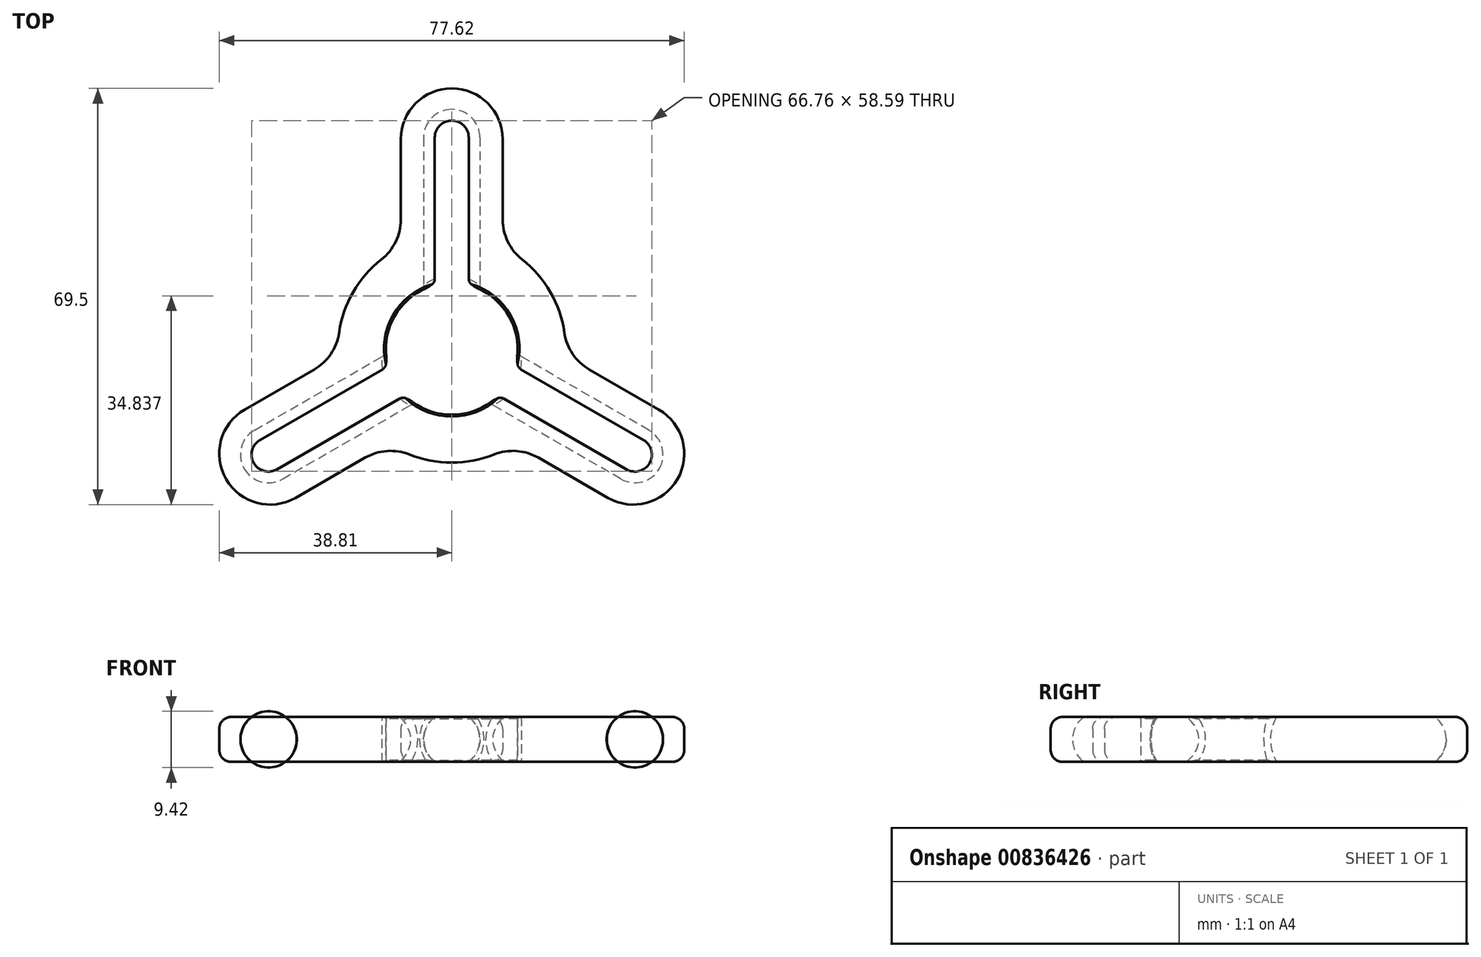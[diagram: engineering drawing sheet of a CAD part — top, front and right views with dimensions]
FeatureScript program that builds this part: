
annotation { "Feature Type Name" : "Feature", "Feature Type Description" : "" }
export const myFeature = defineFeature(function(context is Context, id is Id, definition is map)
    precondition{}
    {
        {
            var Q0;
            Q0=qCreatedBy(makeId("Top.planeOp"),FACE);
            var sketch = newSketch(context, id + "F0", { "sketchPlane" : qUnion([Q0])});
            skLineSegment(sketch, "E0", {"start": v(-9.53, 5.5) * mm, "end": v(0, 0) * mm, "construction": true});
            skLineSegment(sketch, "E1", {"start": v(0, 0) * mm, "end": v(9.53, 5.5) * mm, "construction": true});
            skArc(sketch, "E2", {"start": v(9.53, 5.5) * mm, "mid": v(0, 11) * mm, "end": v(-9.53, 5.5) * mm});
            skLineSegment(sketch, "E3", {"start": v(0, 0) * mm, "end": v(0, 11) * mm, "construction": true});
            skLineSegment(sketch, "E4", {"start": v(-9.53, 5.5) * mm, "end": v(-16.45, 9.5) * mm});
            skLineSegment(sketch, "E5", {"start": v(9.53, 5.5) * mm, "end": v(21.03, 12.14) * mm});
            skLineSegment(sketch, "E6", {"start": v(-8.5, 17) * mm, "end": v(-8.5, 35) * mm});
            skLineSegment(sketch, "E7", {"start": v(8.5, 35) * mm, "end": v(8.5, 17) * mm});
            skArc(sketch, "E8", {"start": v(-16.45, 9.5) * mm, "mid": v(-13.03, 13.83) * mm, "end": v(-8.5, 17) * mm});
            skArc(sketch, "E9", {"start": v(-8.5, 35) * mm, "mid": v(0, 43.5) * mm, "end": v(8.5, 35) * mm});
            skArc(sketch, "E10.trimOffspring", {"start": v(8.5, 17) * mm, "mid": v(13.03, 13.83) * mm, "end": v(16.45, 9.5) * mm});
            skSolve(sketch);
        }
        {
            var Q0;
            Q0=qSketchRegion(id+"F0",true);
            extrude(context, id + "F1", {"entities" : qUnion([Q0]), "depth" : 3.75 * mm, "offsetDistance" : 25 * mm, "hasSecondDirection" : true, "secondDirectionOppositeDirection" : true, "secondDirectionDepth" : 3.75 * mm});
        }
        {
            var Q0;
            Q0=qCreatedBy(makeId("Front.planeOp"),FACE);
            var sketch = newSketch(context, id + "F2", { "sketchPlane" : qUnion([Q0])});
            skCircle(sketch, "E11", {"center": v(0, 0) * mm, "radius": 4.7 * mm});
            skSolve(sketch);
        }
        {
            var Q0;
            Q0=qCreatedBy(makeId("Front.planeOp"),FACE);
            var sketch = newSketch(context, id + "F3", { "sketchPlane" : qUnion([Q0])});
            skLineSegment(sketch, "E12", {"start": v(0, 0) * mm, "end": v(0, 24.93) * mm});
            skSolve(sketch);
        }
        {
            var Q0;
            Q0=qSketchRegion(id+"F2",true);
            extrude(context, id + "F4", {"entities" : qUnion([Q0]), "oppositeDirection" : true, "depth" : 40 * mm, "offsetDistance" : 25 * mm});
        }
        {
            var Q0;
            Q0=makeQuery(id+"F4.opExtrude","CAP_EDGE",EDGE,{"disambiguationData":[OSD([sQuery(id+"F2.wireOp",EDGE,"E11")])],"isStart":false});
            fillet(context, id + "F5", {"entities" : qUnion([Q0]), "radius" : 4.7 * mm, "tangentPropagation" : true, "allowEdgeOverflow" : false});
        }
        {
            var Q0;
            Q0=makeQuery(id+"F1.opExtrude","SWEPT_EDGE",EDGE,{"disambiguationData":[OSD([sQuery(id+"F0.wireOp",EDGE,"E6"),sQuery(id+"F0.wireOp",EDGE,"E8")])]});
            var Q1;
            Q1=makeQuery(id+"F1.opExtrude","SWEPT_EDGE",EDGE,{"disambiguationData":[OSD([sQuery(id+"F0.wireOp",EDGE,"E7"),sQuery(id+"F0.wireOp",EDGE,"E10.trimOffspring")])]});
            fillet(context, id + "F6", {"entities" : qUnion([Q0, Q1]), "radius" : 8.5 * mm, "tangentPropagation" : true, "allowEdgeOverflow" : false});
        }
        {
            var Q0;
            Q0=makeQuery(id+"F4.opExtrude","SWEPT_BODY",BODY,{"disambiguationData":[OSD([sQuery(id+"F2.wireOp",EDGE,"E11")])]});
            var Q1;
            Q1=makeQuery(id+"F1.opExtrude","SWEPT_BODY",BODY,{"disambiguationData":[OSD([sQuery(id+"F0.wireOp",EDGE,"E2"),sQuery(id+"F0.wireOp",EDGE,"E4"),sQuery(id+"F0.wireOp",EDGE,"E5"),sQuery(id+"F0.wireOp",EDGE,"E6"),sQuery(id+"F0.wireOp",EDGE,"E7"),sQuery(id+"F0.wireOp",EDGE,"E8"),sQuery(id+"F0.wireOp",EDGE,"E9"),sQuery(id+"F0.wireOp",EDGE,"E10.trimOffspring")])]});
            booleanBodies(context, id + "F7", {"operationType" : BooleanOperationType.SUBTRACTION, "tools" : qUnion([Q0]), "targets" : qUnion([Q1])});
        }
        {
            var Q0;
            {var subQ0=sQuery(id+"F0.wireOp",EDGE,"E2");var subQ1=sQuery(id+"F0.wireOp",EDGE,"E4");Q0=makeQuery(id+"F7.opBoolean","SPLIT",EDGE,{"disambiguationData":[TD([makeQuery(id+"F1.opExtrude","SWEPT_FACE",FACE,{"disambiguationData":[OSD([subQ1])]})])],"derivedFrom":makeQuery(id+"F1.opExtrude","CAP_EDGE",EDGE,{"disambiguationData":[OSD([subQ0])],"isStart":false})});}
            var Q1;
            {var subQ0=sQuery(id+"F0.wireOp",EDGE,"E2");var subQ1=sQuery(id+"F0.wireOp",EDGE,"E4");Q1=makeQuery(id+"F7.opBoolean","SPLIT",EDGE,{"disambiguationData":[TD([makeQuery(id+"F1.opExtrude","SWEPT_FACE",FACE,{"disambiguationData":[OSD([subQ1])]})])],"derivedFrom":makeQuery(id+"F1.opExtrude","CAP_EDGE",EDGE,{"disambiguationData":[OSD([subQ0])],"isStart":true})});}
            var Q2;
            {var subQ0=sQuery(id+"F0.wireOp",EDGE,"E2");var subQ1=sQuery(id+"F0.wireOp",EDGE,"E5");Q2=makeQuery(id+"F7.opBoolean","SPLIT",EDGE,{"disambiguationData":[TD([makeQuery(id+"F1.opExtrude","SWEPT_FACE",FACE,{"disambiguationData":[OSD([subQ1])]})])],"derivedFrom":makeQuery(id+"F1.opExtrude","CAP_EDGE",EDGE,{"disambiguationData":[OSD([subQ0])],"isStart":true})});}
            var Q3;
            {var subQ0=sQuery(id+"F0.wireOp",EDGE,"E2");var subQ1=sQuery(id+"F0.wireOp",EDGE,"E5");Q3=makeQuery(id+"F7.opBoolean","SPLIT",EDGE,{"disambiguationData":[TD([makeQuery(id+"F1.opExtrude","SWEPT_FACE",FACE,{"disambiguationData":[OSD([subQ1])]})])],"derivedFrom":makeQuery(id+"F1.opExtrude","CAP_EDGE",EDGE,{"disambiguationData":[OSD([subQ0])],"isStart":false})});}
            chamfer(context, id + "F8", {"entities" : qUnion([Q0, Q1, Q2, Q3]), "width" : 0.3 * mm, "tangentPropagation" : true});
        }
        {
            var Q0;
            Q0=makeQuery(id+"F7.opBoolean","INTERSECT",EDGE,{"disambiguationData":[OD(1.0)],"derivedFrom":[makeQuery(id+"F1.opExtrude","SWEPT_FACE",FACE,{"disambiguationData":[OSD([sQuery(id+"F0.wireOp",EDGE,"E2")])]}),makeQuery(id+"F4.opExtrude","SWEPT_FACE",FACE,{"disambiguationData":[OSD([sQuery(id+"F2.wireOp",EDGE,"E11")])]})]});
            var Q1;
            Q1=makeQuery(id+"F7.opBoolean","INTERSECT",EDGE,{"disambiguationData":[OD(0.0)],"derivedFrom":[makeQuery(id+"F1.opExtrude","SWEPT_FACE",FACE,{"disambiguationData":[OSD([sQuery(id+"F0.wireOp",EDGE,"E2")])]}),makeQuery(id+"F4.opExtrude","SWEPT_FACE",FACE,{"disambiguationData":[OSD([sQuery(id+"F2.wireOp",EDGE,"E11")])]})]});
            fillet(context, id + "F9", {"entities" : qUnion([Q0, Q1]), "radius" : 1.2 * mm, "tangentPropagation" : true, "allowEdgeOverflow" : false});
        }
        {
            var Q0;
            Q0=makeQuery(id+"F1.opExtrude","SWEPT_BODY",BODY,{"disambiguationData":[OSD([sQuery(id+"F0.wireOp",EDGE,"E2"),sQuery(id+"F0.wireOp",EDGE,"E4"),sQuery(id+"F0.wireOp",EDGE,"E5"),sQuery(id+"F0.wireOp",EDGE,"E6"),sQuery(id+"F0.wireOp",EDGE,"E7"),sQuery(id+"F0.wireOp",EDGE,"E8"),sQuery(id+"F0.wireOp",EDGE,"E9"),sQuery(id+"F0.wireOp",EDGE,"E10.trimOffspring")])]});
            var Q1;
            Q1=sQuery(id+"F3.wireOp",EDGE,"E12");
            circularPattern(context, id + "F10", {"operationType" : NewBodyOperationType.ADD, "entities" : qUnion([Q0]), "axis" : qUnion([Q1]), "angle" : 360 * degree, "instanceCount" : 3, "equalSpace" : true});
        }
        {
            var Q0;
            Q0=makeQuery(id+"F1.opExtrude","CAP_EDGE",EDGE,{"disambiguationData":[OSD([sQuery(id+"F0.wireOp",EDGE,"E6")])],"isStart":false});
            var Q1;
            Q1=makeQuery(id+"F10.opPattern","COPY",EDGE,{"derivedFrom":makeQuery(id+"F1.opExtrude","CAP_EDGE",EDGE,{"disambiguationData":[OSD([sQuery(id+"F0.wireOp",EDGE,"E6")])],"isStart":true}),"instanceName":"1"});
            fillet(context, id + "F11", {"entities" : qUnion([Q0, Q1]), "radius" : 2 * mm, "tangentPropagation" : true, "allowEdgeOverflow" : false});
        }
    });
